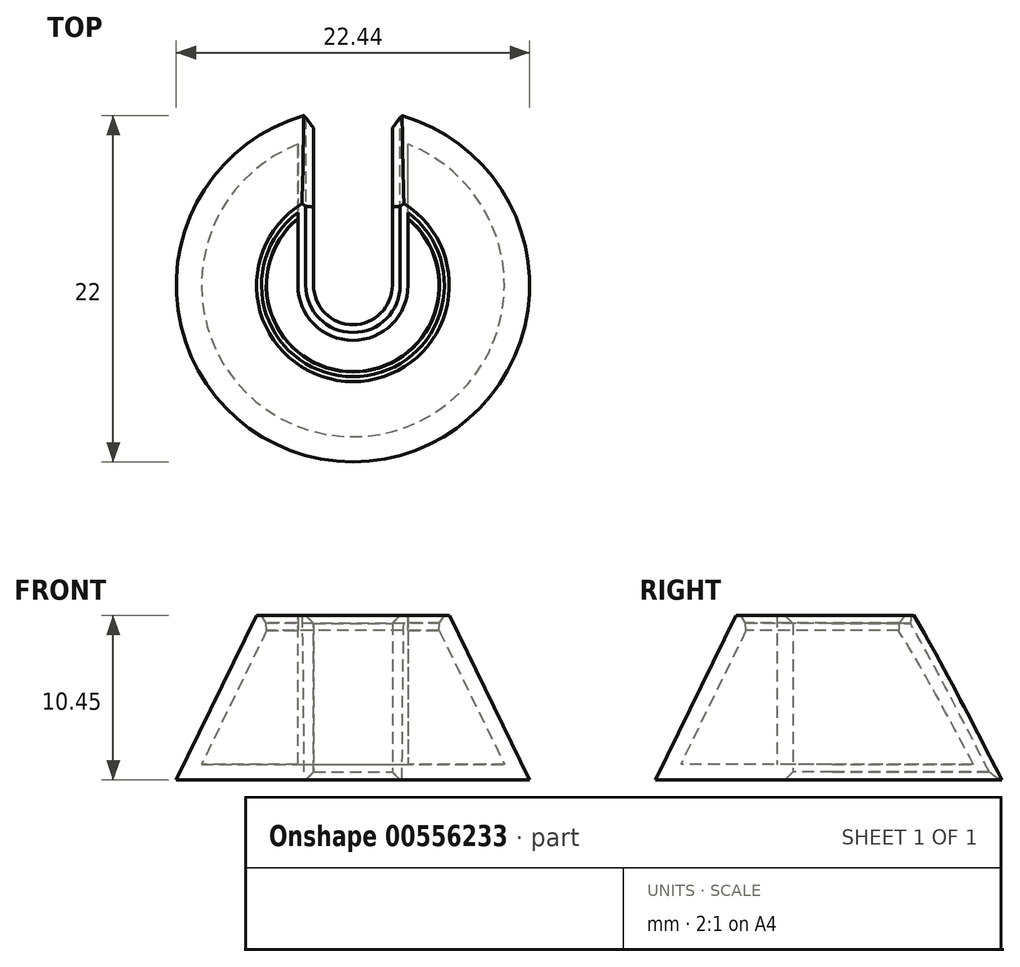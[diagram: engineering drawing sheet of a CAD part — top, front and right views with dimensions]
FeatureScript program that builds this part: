
annotation { "Feature Type Name" : "Feature", "Feature Type Description" : "" }
export const myFeature = defineFeature(function(context is Context, id is Id, definition is map)
    precondition{}
    {
        {
            var Q0;
            Q0=qCreatedBy(makeId("Top.planeOp"),FACE);
            var sketch = newSketch(context, id + "F0", { "sketchPlane" : qUnion([Q0])});
            skCircle(sketch, "E0", {"center": v(0, 0) * mm, "radius": 11.22 * mm});
            skCircle(sketch, "E1", {"center": v(0, 0) * mm, "radius": 2.5 * mm});
            skLineSegment(sketch, "E2", {"start": v(-2.5, 0) * mm, "end": v(2.5, 0) * mm});
            skLineSegment(sketch, "E3", {"start": v(-2.5, 0) * mm, "end": v(-2.5, 10.94) * mm});
            skLineSegment(sketch, "E4", {"start": v(2.5, 0) * mm, "end": v(2.5, 10.94) * mm});
            skSolve(sketch);
        }
        {
            var Q0;
            {var subQ0=sQuery(id+"F0.wireOp",EDGE,"E3");Q0=makeQuery(id+"F0.imprint","IMPRINT",FACE,{"disambiguationData":[TD([[makeQuery(id+"F0.imprint","IMPRINT",EDGE,{"derivedFrom":subQ0}),1.0]])]});}
            extrude(context, id + "F1", {"entities" : qUnion([Q0]), "depth" : 10.45 * mm, "offsetDistance" : 25 * mm});
        }
        {
            var Q0;
            Q0=makeQuery(id+"F1.opExtrude","CAP_EDGE",EDGE,{"disambiguationData":[OSD([sQuery(id+"F0.wireOp",EDGE,"E0")])],"isStart":false});
            chamfer(context, id + "F2", {"entities" : qUnion([Q0]), "chamferType" : ChamferType.TWO_OFFSETS, "width1" : 5.1 * mm, "oppositeDirection" : false, "width2" : 10.45 * mm, "tangentPropagation" : true});
        }
        {
            var Q0;
            Q0=makeQuery(id+"F1.opExtrude","CAP_FACE",FACE,{"disambiguationData":[OSD([sQuery(id+"F0.wireOp",EDGE,"E0"),sQuery(id+"F0.wireOp",EDGE,"E1"),sQuery(id+"F0.wireOp",EDGE,"E3"),sQuery(id+"F0.wireOp",EDGE,"E4")])],"isStart":false});
            shell(context, id + "F3", {"entities" : qUnion([Q0]), "thickness" : 1 * mm});
        }
        {
            var Q0;
            Q0=makeQuery(id+"F1.opExtrude","CAP_EDGE",EDGE,{"disambiguationData":[OSD([sQuery(id+"F0.wireOp",EDGE,"E1")])],"isStart":false});
            var Q1;
            Q1=makeQuery(id+"F1.opExtrude","CAP_EDGE",EDGE,{"disambiguationData":[OSD([sQuery(id+"F0.wireOp",EDGE,"E1")])],"isStart":true});
            var Q2;
            Q2=makeQuery(id+"F2.opChamfer","BLEND_EDGE",EDGE,{"blendedFrom":[makeQuery(id+"F1.opExtrude","CAP_EDGE",EDGE,{"disambiguationData":[OSD([sQuery(id+"F0.wireOp",EDGE,"E0")])],"isStart":false}),makeQuery(id+"F1.opExtrude","SWEPT_FACE",FACE,{"disambiguationData":[OSD([sQuery(id+"F0.wireOp",EDGE,"E4")])]})],"blendedInto":[makeQuery(id+"F1.opExtrude","SWEPT_FACE",FACE,{"disambiguationData":[OSD([sQuery(id+"F0.wireOp",EDGE,"E4")])]})]});
            var Q3;
            Q3=makeQuery(id+"F2.opChamfer","BLEND_EDGE",EDGE,{"blendedFrom":[makeQuery(id+"F1.opExtrude","CAP_EDGE",EDGE,{"disambiguationData":[OSD([sQuery(id+"F0.wireOp",EDGE,"E0")])],"isStart":false}),makeQuery(id+"F1.opExtrude","SWEPT_FACE",FACE,{"disambiguationData":[OSD([sQuery(id+"F0.wireOp",EDGE,"E3")])]})],"blendedInto":[makeQuery(id+"F1.opExtrude","SWEPT_FACE",FACE,{"disambiguationData":[OSD([sQuery(id+"F0.wireOp",EDGE,"E3")])]})]});
            chamfer(context, id + "F4", {"entities" : qUnion([Q0, Q1, Q2, Q3]), "width" : 0.5 * mm, "tangentPropagation" : true});
        }
        {
            var Q0;
            {var subQ0=sQuery(id+"F0.wireOp",EDGE,"E4");var subQ1=sQuery(id+"F0.wireOp",EDGE,"E3");var subQ2=sQuery(id+"F0.wireOp",EDGE,"E1");var subQ3=sQuery(id+"F0.wireOp",EDGE,"E0");Q0=makeQuery(id+"F3.opShell","OFFSET_EDGE",EDGE,{"disambiguationData":[OSD([subQ3,subQ2,subQ1,subQ0]),TDD([makeQuery(id+"F2.opChamfer","BLEND_EDGE",EDGE,{"blendedFrom":[makeQuery(id+"F1.opExtrude","CAP_EDGE",EDGE,{"disambiguationData":[OSD([subQ3])],"isStart":false}),makeQuery(id+"F1.opExtrude","CAP_FACE",FACE,{"disambiguationData":[OSD([subQ3,subQ2,subQ1,subQ0])],"isStart":false})],"blendedInto":[makeQuery(id+"F1.opExtrude","CAP_FACE",FACE,{"disambiguationData":[OSD([subQ3,subQ2,subQ1,subQ0])],"isStart":false})]})])]});}
            chamfer(context, id + "F5", {"entities" : qUnion([Q0]), "width" : 0.5 * mm, "tangentPropagation" : true});
        }
        {
            var Q0;
            {var subQ0=sQuery(id+"F0.wireOp",EDGE,"E0");var subQ1=sQuery(id+"F0.wireOp",EDGE,"E4");var subQ2=sQuery(id+"F0.wireOp",EDGE,"E3");var subQ3=sQuery(id+"F0.wireOp",EDGE,"E1");Q0=makeQuery(id+"F5.opChamfer","BLEND_EDGE",EDGE,{"blendedFrom":[makeQuery(id+"F3.opShell","OFFSET_EDGE",EDGE,{"disambiguationData":[OSD([subQ0,subQ3,subQ2,subQ1]),TDD([makeQuery(id+"F2.opChamfer","BLEND_EDGE",EDGE,{"blendedFrom":[makeQuery(id+"F1.opExtrude","CAP_EDGE",EDGE,{"disambiguationData":[OSD([subQ0])],"isStart":false}),makeQuery(id+"F1.opExtrude","CAP_FACE",FACE,{"disambiguationData":[OSD([subQ0,subQ3,subQ2,subQ1])],"isStart":false})],"blendedInto":[makeQuery(id+"F1.opExtrude","CAP_FACE",FACE,{"disambiguationData":[OSD([subQ0,subQ3,subQ2,subQ1])],"isStart":false})]})])]}),makeQuery(id+"F3.opShell","OFFSET_FACE",FACE,{"disambiguationData":[OSD([subQ0])]})],"blendedInto":[makeQuery(id+"F3.opShell","OFFSET_FACE",FACE,{"disambiguationData":[OSD([subQ0])]})]});}
            chamfer(context, id + "F6", {"entities" : qUnion([Q0]), "width" : 0.5 * mm, "tangentPropagation" : true});
        }
    });
